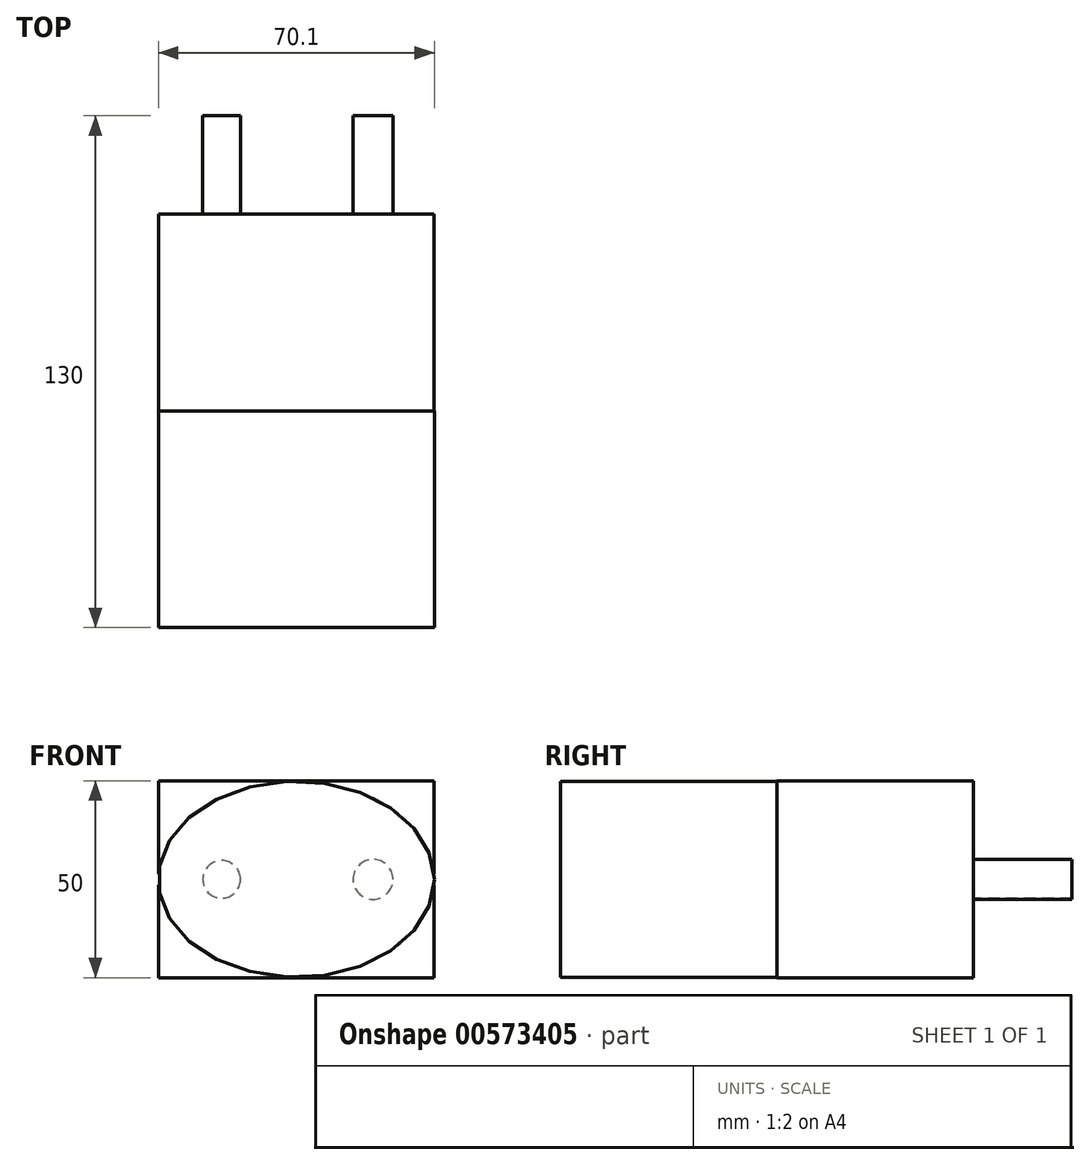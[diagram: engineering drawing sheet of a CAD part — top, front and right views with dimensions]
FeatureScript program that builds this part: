
annotation { "Feature Type Name" : "Feature", "Feature Type Description" : "" }
export const myFeature = defineFeature(function(context is Context, id is Id, definition is map)
    precondition{}
    {
        {
            var Q0;
            Q0=qCreatedBy(makeId("Top.planeOp"),FACE);
            var sketch = newSketch(context, id + "F0", { "sketchPlane" : qUnion([Q0])});
            skLineSegment(sketch, "E0.bottom", {"start": v(0, 19) * mm, "end": v(70, 19) * mm});
            skLineSegment(sketch, "E0.top", {"start": v(0, -31) * mm, "end": v(70, -31) * mm});
            skLineSegment(sketch, "E0.left", {"start": v(0, 19) * mm, "end": v(0, -31) * mm});
            skLineSegment(sketch, "E0.right", {"start": v(70, 19) * mm, "end": v(70, -31) * mm});
            skSolve(sketch);
        }
        {
            var Q0;
            Q0 = qSketchRegion(id + "F0", true);
            extrude(context, id + "F1", {"entities" : qUnion([Q0]), "depth" : 50 * mm, "offsetDistance" : 25 * mm});
        }
        {
            var Q0;
            Q0=makeQuery(id+"F1.opExtrude","SWEPT_FACE",FACE,{"disambiguationData":[OSD([sQuery(id+"F0.wireOp",EDGE,"E0.top")])]});
            var sketch = newSketch(context, id + "F2", { "sketchPlane" : qUnion([Q0])});
            skPoint(sketch, "E1.endSnap0", {"position": v(35, 0) * mm});
            skEllipse(sketch, "E2", {"center": v(35, 25) * mm, "majorRadius": 35.05 * mm, "minorRadius": 24.88 * mm, "majorAxis": v(1, 0)});
            skLineSegment(sketch, "E3.trimOffspring", {"start": v(35, 0.12) * mm, "end": v(35, 0) * mm});
            skPoint(sketch, "E4.orphan", {"position": v(35, -8.87) * mm});
            skSolve(sketch);
        }
        {
            var Q0;
            Q0 = qSketchRegion(id + "F2", true);
            extrude(context, id + "F3", {"entities" : qUnion([Q0]), "operationType" : NewBodyOperationType.ADD, "depth" : 55 * mm, "offsetDistance" : 25 * mm});
        }
        {
            var Q0;
            Q0=makeQuery(id+"F1.opExtrude","SWEPT_FACE",FACE,{"disambiguationData":[OSD([sQuery(id+"F0.wireOp",EDGE,"E0.bottom")])]});
            var sketch = newSketch(context, id + "F4", { "sketchPlane" : qUnion([Q0])});
            skLineSegment(sketch, "E5", {"start": v(-70, 50) * mm, "end": v(-79.62, 50) * mm});
            skLineSegment(sketch, "E6", {"start": v(-79.62, 50) * mm, "end": v(-79.62, 25) * mm});
            skLineSegment(sketch, "E7", {"start": v(-79.62, 25) * mm, "end": v(28.69, 25) * mm});
            skCircle(sketch, "E8", {"center": v(-54.47, 25) * mm, "radius": 5.1 * mm});
            skCircle(sketch, "E9", {"center": v(-16.03, 25) * mm, "radius": 4.8 * mm});
            skSolve(sketch);
        }
        {
            var Q0;
            Q0 = qSketchRegion(id + "F4", true);
            extrude(context, id + "F5", {"entities" : qUnion([Q0]), "operationType" : NewBodyOperationType.ADD, "depth" : 25 * mm, "offsetDistance" : 25 * mm});
        }
    });
